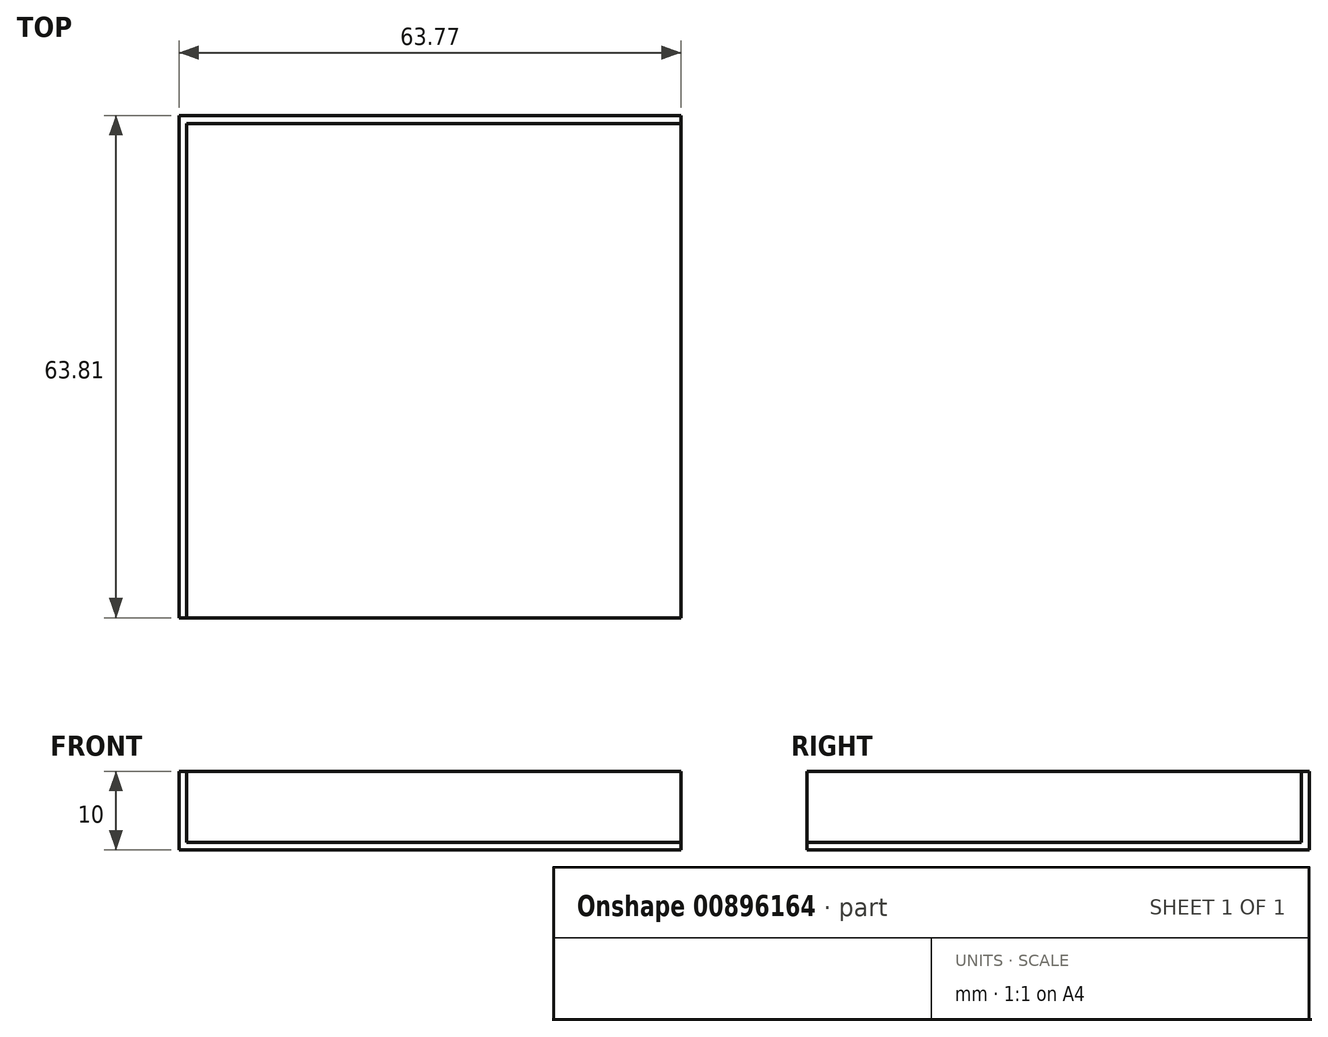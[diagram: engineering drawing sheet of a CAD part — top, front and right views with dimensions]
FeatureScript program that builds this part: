
annotation { "Feature Type Name" : "Feature", "Feature Type Description" : "" }
export const myFeature = defineFeature(function(context is Context, id is Id, definition is map)
    precondition{}
    {
        {
            var Q0;
            Q0=qCreatedBy(makeId("Top.planeOp"),FACE);
            var sketch = newSketch(context, id + "F0", { "sketchPlane" : qUnion([Q0])});
            skLineSegment(sketch, "E0.bottom", {"start": v(23.5, -27.89) * mm, "end": v(-40.28, -27.89) * mm});
            skLineSegment(sketch, "E0.top", {"start": v(23.5, 35.92) * mm, "end": v(-40.28, 35.92) * mm});
            skLineSegment(sketch, "E0.left", {"start": v(23.5, -27.89) * mm, "end": v(23.5, 35.92) * mm});
            skLineSegment(sketch, "E0.right", {"start": v(-40.28, -27.89) * mm, "end": v(-40.28, 35.92) * mm});
            skSolve(sketch);
        }
        {
            var Q0;
            Q0 = qSketchRegion(id + "F0", true);
            extrude(context, id + "F1", {"entities" : qUnion([Q0]), "depth" : 10 * mm, "offsetDistance" : 25.4 * mm});
        }
        {
            var Q0;
            Q0=makeQuery(id+"F1.opExtrude","SWEPT_FACE",FACE,{"disambiguationData":[OSD([sQuery(id+"F0.wireOp",EDGE,"E0.left")])]});
            var Q1;
            Q1=makeQuery(id+"F1.opExtrude","SWEPT_FACE",FACE,{"disambiguationData":[OSD([sQuery(id+"F0.wireOp",EDGE,"E0.bottom")])]});
            var Q2;
            Q2=makeQuery(id+"F1.opExtrude","CAP_FACE",FACE,{"disambiguationData":[OSD([sQuery(id+"F0.wireOp",EDGE,"E0.bottom"),sQuery(id+"F0.wireOp",EDGE,"E0.top"),sQuery(id+"F0.wireOp",EDGE,"E0.left"),sQuery(id+"F0.wireOp",EDGE,"E0.right")])],"isStart":false});
            shell(context, id + "F2", {"entities" : qUnion([Q0, Q1, Q2]), "thickness" : 1 * mm});
        }
    });
